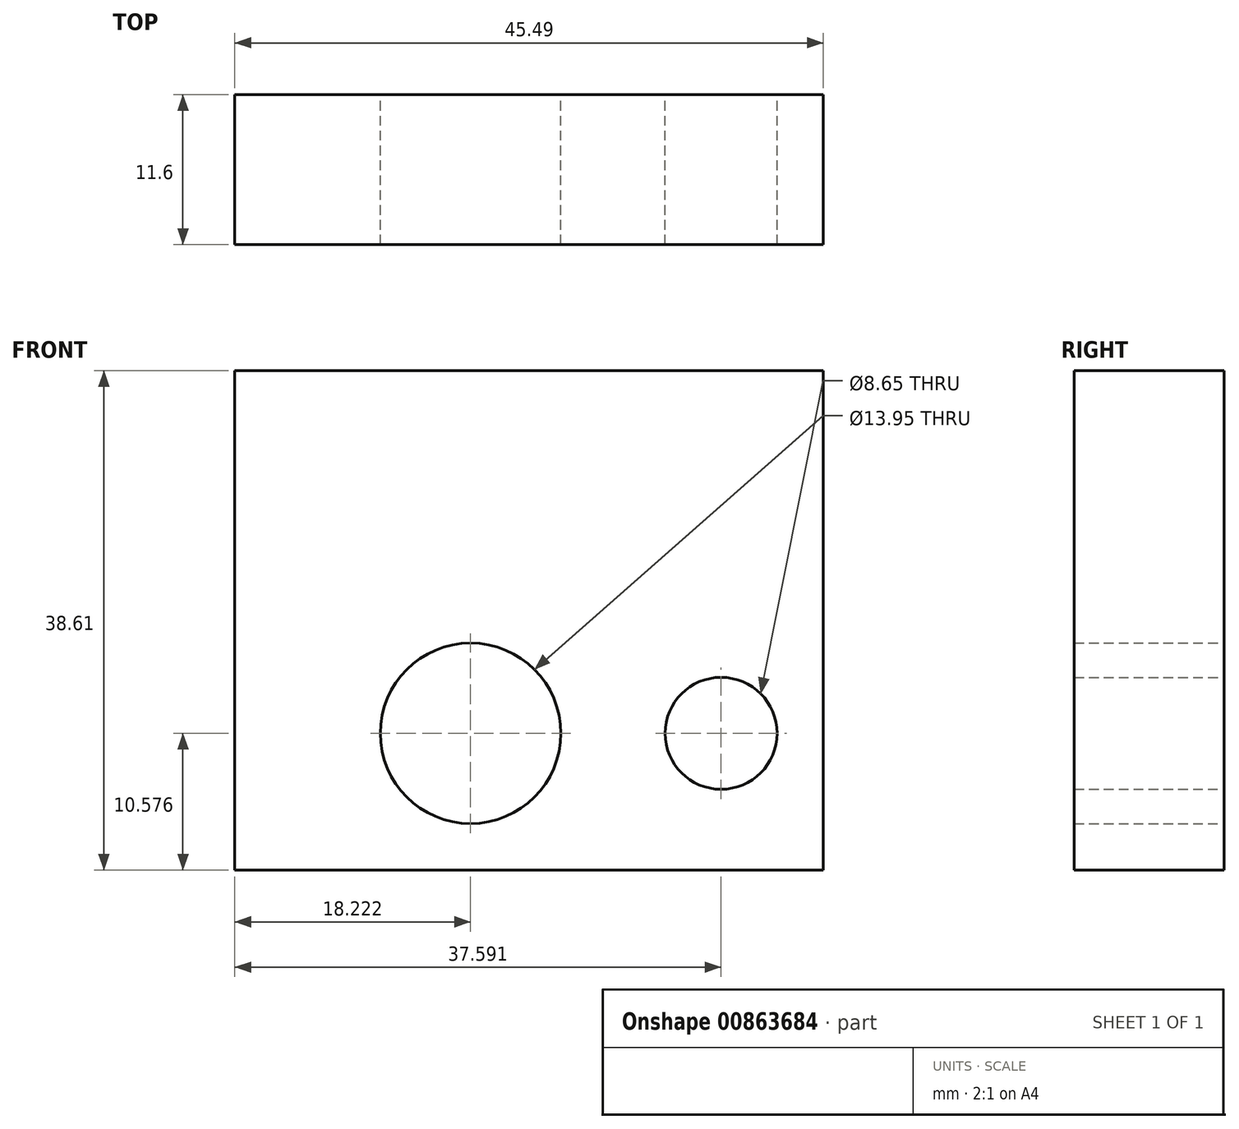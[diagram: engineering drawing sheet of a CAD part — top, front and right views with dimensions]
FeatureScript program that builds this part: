
annotation { "Feature Type Name" : "Feature", "Feature Type Description" : "" }
export const myFeature = defineFeature(function(context is Context, id is Id, definition is map)
    precondition{}
    {
        {
            var Q0;
            Q0=qCreatedBy(makeId("Front.planeOp"),FACE);
            var sketch = newSketch(context, id + "F0", { "sketchPlane" : qUnion([Q0])});
            skLineSegment(sketch, "E0", {"start": v(0, 0) * mm, "end": v(45.5, 0) * mm});
            skLineSegment(sketch, "E1", {"start": v(45.5, 0) * mm, "end": v(45.5, 38.61) * mm});
            skLineSegment(sketch, "E2", {"start": v(45.5, 38.61) * mm, "end": v(0, 38.61) * mm});
            skLineSegment(sketch, "E3", {"start": v(0, 38.61) * mm, "end": v(0, 0) * mm});
            skSolve(sketch);
        }
        {
            var Q0;
            Q0=makeQuery(id+"F0.imprint","IMPRINT",FACE,{"disambiguationData":[TD([[makeQuery(id+"F0.imprint","IMPRINT",EDGE,{"derivedFrom":sQuery(id+"F0.wireOp",EDGE,"E0")}),1.0]])]});
            extrude(context, id + "F1", {"entities" : qUnion([Q0]), "depth" : 11.6 * mm, "offsetDistance" : 25 * mm});
        }
        {
            var Q0;
            Q0=makeQuery(id+"F1.opExtrude","CAP_FACE",FACE,{"disambiguationData":[OSD([sQuery(id+"F0.wireOp",EDGE,"E0"),sQuery(id+"F0.wireOp",EDGE,"E1"),sQuery(id+"F0.wireOp",EDGE,"E2"),sQuery(id+"F0.wireOp",EDGE,"E3")])],"isStart":true});
            var sketch = newSketch(context, id + "F2", { "sketchPlane" : qUnion([Q0])});
            skCircle(sketch, "E4", {"center": v(-37.6, 10.58) * mm, "radius": 4.33 * mm});
            skCircle(sketch, "E5", {"center": v(-18.22, 24.85) * mm, "radius": 5.77 * mm});
            skCircle(sketch, "E6", {"center": v(-37.6, 24.85) * mm, "radius": 4.96 * mm});
            skCircle(sketch, "E7", {"center": v(-18.22, 10.58) * mm, "radius": 6.98 * mm});
            skSolve(sketch);
        }
        {
            var Q0;
            Q0=makeQuery(id+"F2.imprint","IMPRINT",FACE,{"disambiguationData":[TD([[makeQuery(id+"F2.imprint","IMPRINT",EDGE,{"derivedFrom":sQuery(id+"F2.wireOp",EDGE,"E7")}),1.0]])]});
            var Q1;
            Q1=makeQuery(id+"F2.imprint","IMPRINT",FACE,{"disambiguationData":[TD([[makeQuery(id+"F2.imprint","IMPRINT",EDGE,{"derivedFrom":sQuery(id+"F2.wireOp",EDGE,"E4")}),1.0]])]});
            extrude(context, id + "F3", {"entities" : qUnion([Q0, Q1]), "operationType" : NewBodyOperationType.REMOVE, "oppositeDirection" : true, "depth" : 25 * mm, "offsetDistance" : 25 * mm});
        }
    });
